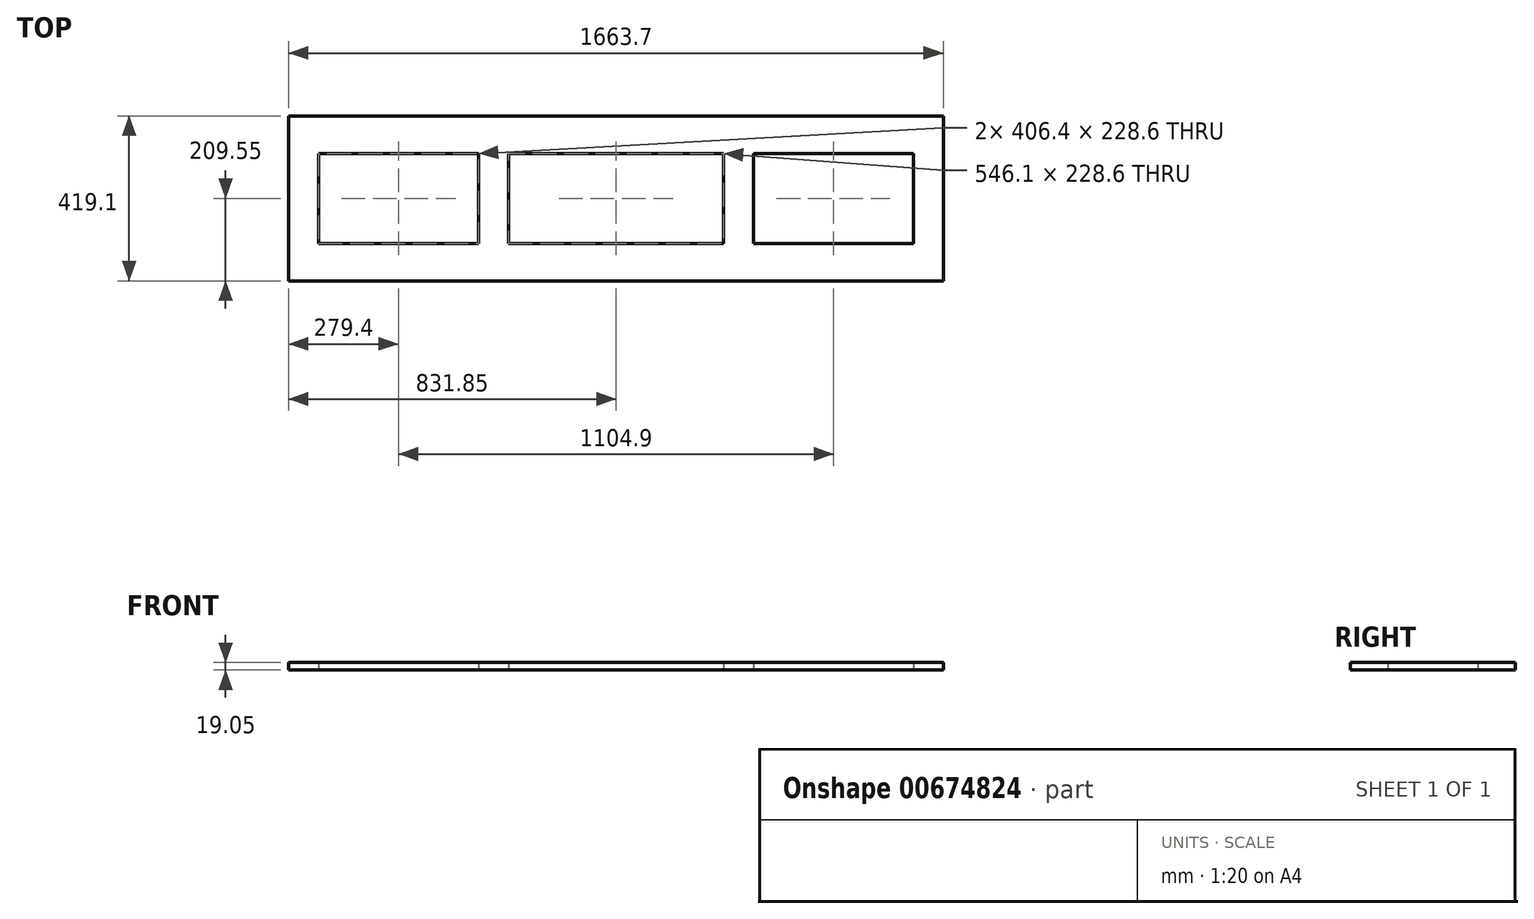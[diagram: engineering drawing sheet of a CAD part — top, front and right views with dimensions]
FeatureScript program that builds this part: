
annotation { "Feature Type Name" : "Feature", "Feature Type Description" : "" }
export const myFeature = defineFeature(function(context is Context, id is Id, definition is map)
    precondition{}
    {
        {
            var Q0;
            Q0=qCreatedBy(makeId("Top.planeOp"),FACE);
            var sketch = newSketch(context, id + "F0", { "sketchPlane" : qUnion([Q0])});
            skLineSegment(sketch, "E0.bottom", {"start": v(-831.85, 209.55) * mm, "end": v(831.85, 209.55) * mm});
            skLineSegment(sketch, "E0.top", {"start": v(-831.85, -209.55) * mm, "end": v(831.85, -209.55) * mm});
            skLineSegment(sketch, "E0.left", {"start": v(-831.85, 209.55) * mm, "end": v(-831.85, -209.55) * mm});
            skLineSegment(sketch, "E0.right", {"start": v(831.85, 209.55) * mm, "end": v(831.85, -209.55) * mm});
            skPoint(sketch, "E0.middle", {"position": v(0, 0) * mm});
            skLineSegment(sketch, "E1.bottom", {"start": v(-273.05, 114.3) * mm, "end": v(273.05, 114.3) * mm});
            skLineSegment(sketch, "E1.top", {"start": v(-273.05, -114.3) * mm, "end": v(273.05, -114.3) * mm});
            skLineSegment(sketch, "E1.left", {"start": v(-273.05, 114.3) * mm, "end": v(-273.05, -114.3) * mm});
            skLineSegment(sketch, "E1.right", {"start": v(273.05, 114.3) * mm, "end": v(273.05, -114.3) * mm});
            skLineSegment(sketch, "E2", {"start": v(-273.05, 114.3) * mm, "end": v(-349.25, 114.3) * mm});
            skLineSegment(sketch, "E3.bottom", {"start": v(-349.25, 114.3) * mm, "end": v(-755.65, 114.3) * mm});
            skLineSegment(sketch, "E3.top", {"start": v(-349.25, -114.3) * mm, "end": v(-755.65, -114.3) * mm});
            skLineSegment(sketch, "E3.left", {"start": v(-349.25, 114.3) * mm, "end": v(-349.25, -114.3) * mm});
            skLineSegment(sketch, "E3.right", {"start": v(-755.65, 114.3) * mm, "end": v(-755.65, -114.3) * mm});
            skLineSegment(sketch, "E4", {"start": v(273.05, 114.3) * mm, "end": v(349.25, 114.3) * mm});
            skLineSegment(sketch, "E5.bottom", {"start": v(349.25, 114.3) * mm, "end": v(755.65, 114.3) * mm});
            skLineSegment(sketch, "E5.top", {"start": v(349.25, -114.3) * mm, "end": v(755.65, -114.3) * mm});
            skLineSegment(sketch, "E5.left", {"start": v(349.25, 114.3) * mm, "end": v(349.25, -114.3) * mm});
            skLineSegment(sketch, "E5.right", {"start": v(755.65, 114.3) * mm, "end": v(755.65, -114.3) * mm});
            skSolve(sketch);
        }
        {
            var Q0;
            Q0=makeQuery(id+"F0.imprint","IMPRINT",FACE,{"disambiguationData":[TD([[makeQuery(id+"F0.imprint","IMPRINT",EDGE,{"derivedFrom":sQuery(id+"F0.wireOp",EDGE,"E0.bottom")}),-1.0]])]});
            extrude(context, id + "F1", {"entities" : qUnion([Q0]), "depth" : 19.05 * mm, "offsetDistance" : 25.4 * mm});
        }
    });
